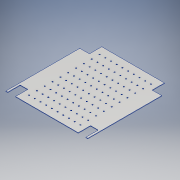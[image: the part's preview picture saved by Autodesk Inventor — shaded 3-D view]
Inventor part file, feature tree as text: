
AUTODESK INVENTOR PART (.ipt)
format: ipt  version: 2017 (Build 210142000, 142)  size: 282,112 bytes
history: native  units: mm
features: extrude x2, sketch x2
ambient origin geometry x8: Origin, YZ Plane, XZ Plane, XY Plane, X Axis, Y Axis, Z Axis, Center Point
bodies: Solid1 (feature_tree)
feature tree (4):
  extrude  "Extrusion1"  Depth=3.175mm TaperAngle=0.0deg
  extrude  "Extrusion2"  Depth=10.0mm
  sketch  "Sketch1"  dims[d0=541.02mm d1=568.96mm d2=12.7mm d6=414.02mm d10=12.7mm d11=487.68mm d14=414.02mm d17=3.175mm d18=0.0mm]
  sketch  "Sketch2"  dims[d19=78.105mm d20=60.325mm d22=78.105mm d23=60.325mm d26=78.105mm d27=78.105mm d28=44.45mm d29=50.8mm d30=78.105mm d31=78.105mm d32=7.5mm d33=37.638182mm d34=51.723636mm d35=100.0mm d37=51.723636mm d38=100.0mm d40=37.638182mm d43=10.0mm d44=0.0mm]
